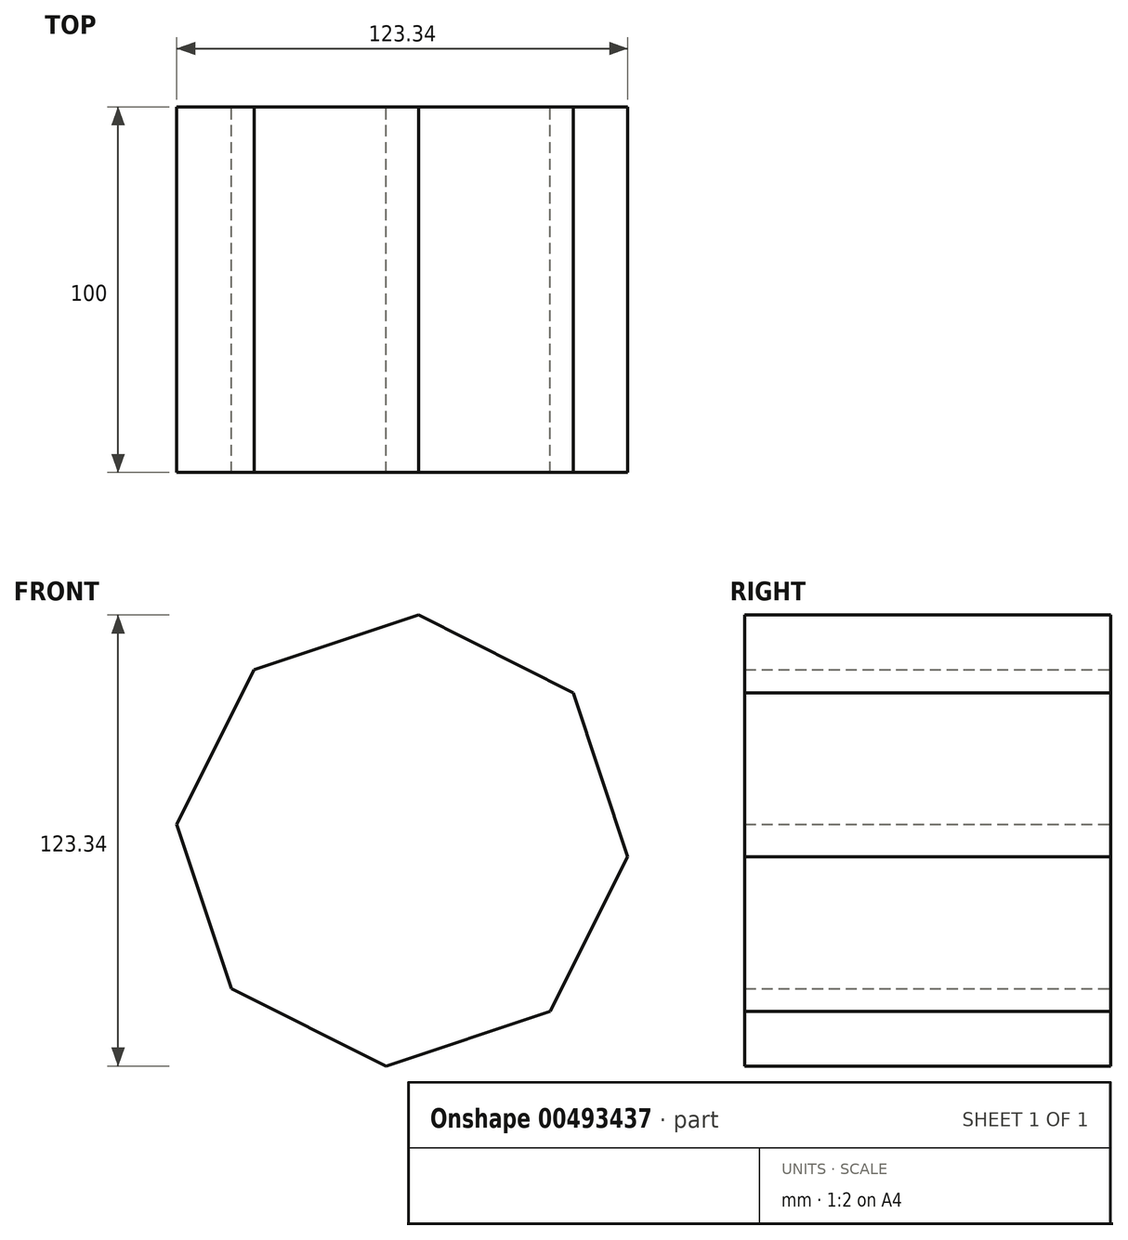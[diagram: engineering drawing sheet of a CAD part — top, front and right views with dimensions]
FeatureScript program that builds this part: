
annotation { "Feature Type Name" : "Feature", "Feature Type Description" : "" }
export const myFeature = defineFeature(function(context is Context, id is Id, definition is map)
    precondition{}
    {
        {
            var Q0;
            Q0=qCreatedBy(makeId("Front.planeOp"),FACE);
            var sketch = newSketch(context, id + "F0", { "sketchPlane" : qUnion([Q0])});
            skCircle(sketch, "E0.cCircle", {"center": v(0, -2.15) * mm, "radius": 61.83 * mm, "construction": true});
            skLineSegment(sketch, "E0.0", {"start": v(46.76, 38.3) * mm, "end": v(61.67, -6.61) * mm});
            skLineSegment(sketch, "E0.1", {"start": v(61.67, -6.61) * mm, "end": v(40.45, -48.91) * mm});
            skLineSegment(sketch, "E0.2", {"start": v(40.45, -48.91) * mm, "end": v(-4.46, -63.82) * mm});
            skLineSegment(sketch, "E0.3", {"start": v(-4.46, -63.82) * mm, "end": v(-46.76, -42.6) * mm});
            skLineSegment(sketch, "E0.4", {"start": v(-46.76, -42.6) * mm, "end": v(-61.67, 2.31) * mm});
            skLineSegment(sketch, "E0.5", {"start": v(-61.67, 2.31) * mm, "end": v(-40.45, 44.61) * mm});
            skLineSegment(sketch, "E0.6", {"start": v(-40.45, 44.61) * mm, "end": v(4.46, 59.52) * mm});
            skLineSegment(sketch, "E0.7", {"start": v(4.46, 59.52) * mm, "end": v(46.76, 38.3) * mm});
            skSolve(sketch);
        }
        {
            var Q0;
            Q0=makeQuery(id+"F0.imprint","IMPRINT",FACE,{"disambiguationData":[TD([[makeQuery(id+"F0.imprint","IMPRINT",EDGE,{"derivedFrom":sQuery(id+"F0.wireOp",EDGE,"E0.0")}),-1.0]])]});
            extrude(context, id + "F1", {"entities" : qUnion([Q0]), "depth" : 100 * mm});
        }
    });
